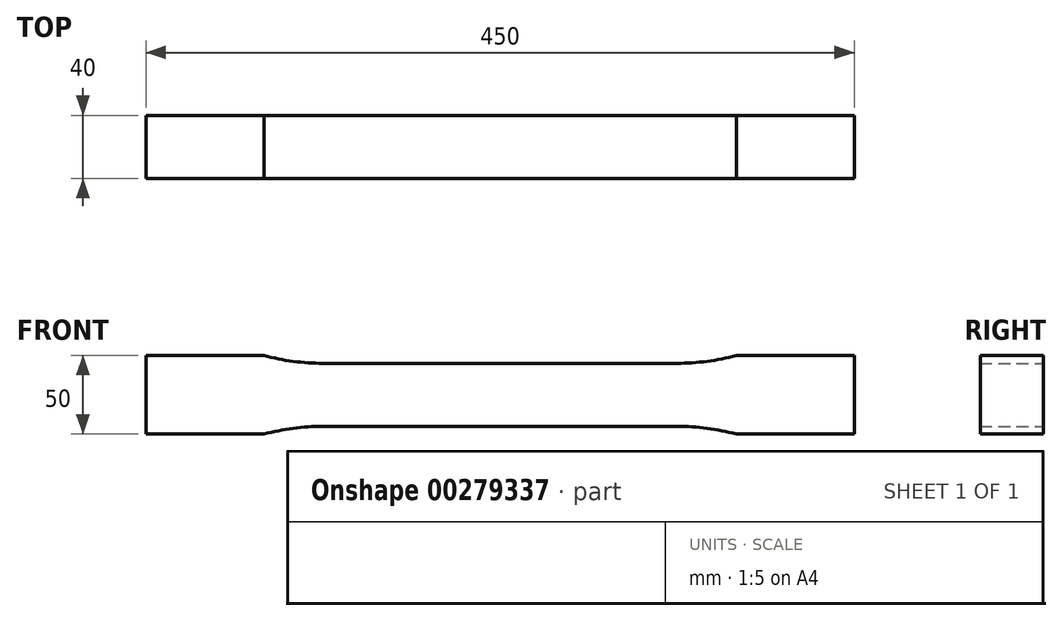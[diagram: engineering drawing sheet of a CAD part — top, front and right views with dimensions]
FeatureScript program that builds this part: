
annotation { "Feature Type Name" : "Feature", "Feature Type Description" : "" }
export const myFeature = defineFeature(function(context is Context, id is Id, definition is map)
    precondition{}
    {
        {
            var Q0;
            Q0=qCreatedBy(makeId("Front.planeOp"),FACE);
            var sketch = newSketch(context, id + "F0", { "sketchPlane" : qUnion([Q0])});
            skLineSegment(sketch, "E0", {"start": v(0, 20) * mm, "end": v(112.5, 20) * mm});
            skArc(sketch, "E1", {"start": v(112.5, 20) * mm, "mid": v(131.42, 21.26) * mm, "end": v(150, 25) * mm});
            skLineSegment(sketch, "E2", {"start": v(150, 25) * mm, "end": v(225, 25) * mm});
            skLineSegment(sketch, "E3", {"start": v(225, 25) * mm, "end": v(225, 0) * mm});
            skLineSegment(sketch, "E4.MirrorCS", {"start": v(0, -20) * mm, "end": v(112.5, -20) * mm});
            skLineSegment(sketch, "E5.MirrorCS", {"start": v(225, -25) * mm, "end": v(225, 0) * mm});
            skLineSegment(sketch, "E6.MirrorCS", {"start": v(150, -25) * mm, "end": v(225, -25) * mm});
            skArc(sketch, "E7.MirrorCS", {"start": v(112.5, -20) * mm, "mid": v(131.42, -21.26) * mm, "end": v(150, -25) * mm});
            skArc(sketch, "E8.MirrorCS", {"start": v(-112.5, -20) * mm, "mid": v(-131.42, -21.26) * mm, "end": v(-150, -25) * mm});
            skLineSegment(sketch, "E9.MirrorCS", {"start": v(-150, -25) * mm, "end": v(-225, -25) * mm});
            skArc(sketch, "E10.MirrorCS", {"start": v(-112.5, 20) * mm, "mid": v(-131.42, 21.26) * mm, "end": v(-150, 25) * mm});
            skLineSegment(sketch, "E11.MirrorCS", {"start": v(-150, 25) * mm, "end": v(-225, 25) * mm});
            skLineSegment(sketch, "E12.MirrorCS", {"start": v(-225, -25) * mm, "end": v(-225, 0) * mm});
            skLineSegment(sketch, "E13.MirrorCS", {"start": v(0, -20) * mm, "end": v(-112.5, -20) * mm});
            skLineSegment(sketch, "E14.MirrorCS", {"start": v(-225, 25) * mm, "end": v(-225, 0) * mm});
            skLineSegment(sketch, "E15.MirrorCS", {"start": v(0, 20) * mm, "end": v(-112.5, 20) * mm});
            skSolve(sketch);
        }
        {
            var Q0;
            Q0=makeQuery(id+"F0.imprint","IMPRINT",FACE,{"disambiguationData":[TD([[makeQuery(id+"F0.imprint","IMPRINT",EDGE,{"derivedFrom":sQuery(id+"F0.wireOp",EDGE,"E0")}),-1.0]])]});
            extrude(context, id + "F1", {"entities" : qUnion([Q0]), "depth" : 40 * mm});
        }
    });
